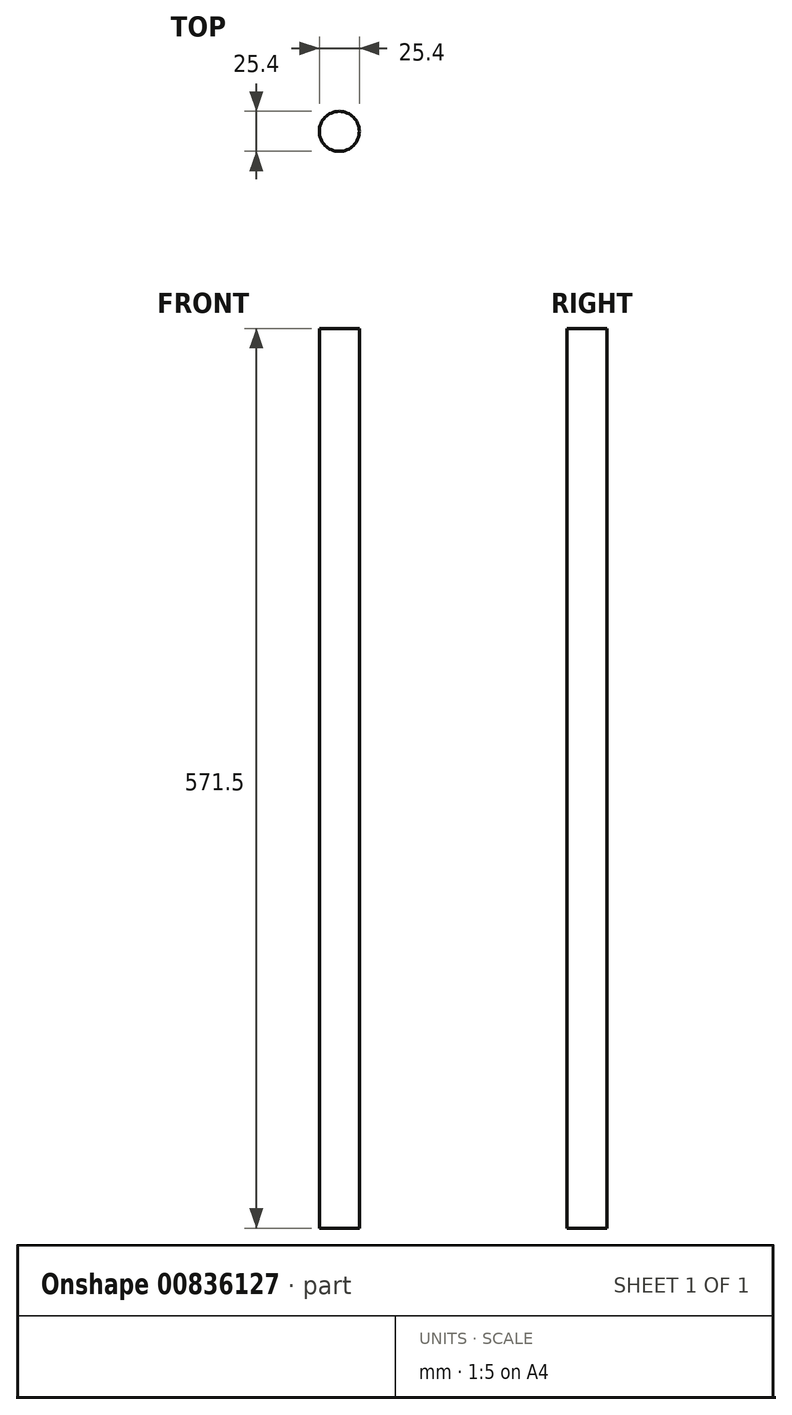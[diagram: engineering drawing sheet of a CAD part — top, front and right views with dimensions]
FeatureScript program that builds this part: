
annotation { "Feature Type Name" : "Feature", "Feature Type Description" : "" }
export const myFeature = defineFeature(function(context is Context, id is Id, definition is map)
    precondition{}
    {
        {
            var Q0;
            Q0=qCreatedBy(makeId("Top.planeOp"),FACE);
            var sketch = newSketch(context, id + "F0", { "sketchPlane" : qUnion([Q0])});
            skCircle(sketch, "E0", {"center": v(0, 0) * mm, "radius": 285.75 * mm});
            skCircle(sketch, "E1", {"center": v(0, 0) * mm, "radius": 12.7 * mm});
            skSolve(sketch);
        }
        {
            var Q0;
            Q0 = qSketchRegion(id + "F0", true);
            var Q1;
            Q1=sQuery(id+"F0.wireOp",EDGE,"E0");
            extrude(context, id + "F1", {"entities" : qUnion([Q0]), "bodyType" : ToolBodyType.SURFACE, "surfaceEntities" : qUnion([Q1]), "depth" : 850.9 * mm, "offsetDistance" : 25.4 * mm});
        }
        {
            var Q0;
            Q0=makeQuery(id+"F0.imprint","IMPRINT",FACE,{"disambiguationData":[TD([[makeQuery(id+"F0.imprint","IMPRINT",EDGE,{"derivedFrom":sQuery(id+"F0.wireOp",EDGE,"E1")}),1.0]])]});
            extrude(context, id + "F2", {"entities" : qUnion([Q0]), "oppositeDirection" : true, "depth" : 571.5 * mm, "offsetDistance" : 25.4 * mm});
        }
        {
            var Q0;
            Q0=qCreatedBy(makeId("Right.planeOp"),FACE);
            var sketch = newSketch(context, id + "F3", { "sketchPlane" : qUnion([Q0])});
            skLineSegment(sketch, "E2", {"start": v(12.66, -570.7) * mm, "end": v(281.8, 0) * mm});
            skSolve(sketch);
        }
        {
            var Q0;
            Q0 = qSketchRegion(id + "F3", true);
            var Q1;
            Q1=sQuery(id+"F3.wireOp",EDGE,"E2");
            var Q2;
            Q2=makeQuery(id+"F2.opExtrude","SWEPT_FACE",FACE,{"disambiguationData":[OSD([sQuery(id+"F0.wireOp",EDGE,"E1")])]});
            revolve(context, id + "F4", {"bodyType" : ToolBodyType.SURFACE, "surfaceOperationType" : NewSurfaceOperationType.NEW, "entities" : qUnion([Q0]), "surfaceEntities" : qUnion([Q1]), "axis" : qUnion([Q2]), "revolveType" : RevolveType.FULL});
        }
    });
